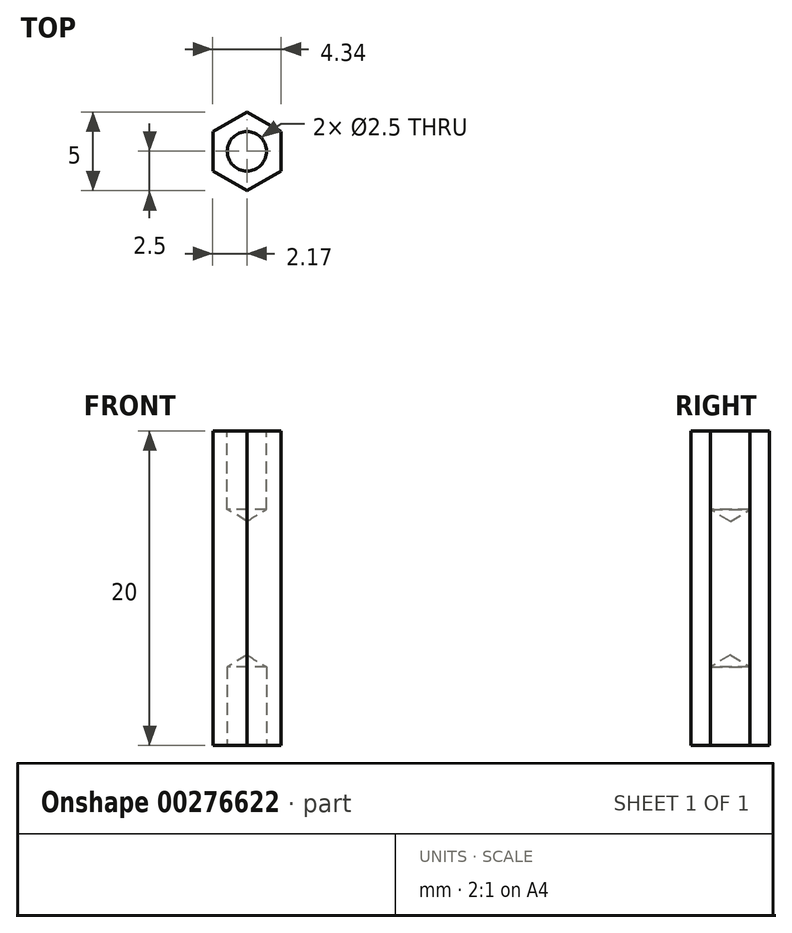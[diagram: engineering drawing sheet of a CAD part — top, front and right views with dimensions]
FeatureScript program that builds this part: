
annotation { "Feature Type Name" : "Feature", "Feature Type Description" : "" }
export const myFeature = defineFeature(function(context is Context, id is Id, definition is map)
    precondition{}
    {
        {
            var Q0;
            Q0=qCreatedBy(makeId("Top.planeOp"),FACE);
            var sketch = newSketch(context, id + "F0", { "sketchPlane" : qUnion([Q0])});
            skCircle(sketch, "E0", {"center": v(0, 0) * mm, "radius": 2.5 * mm, "construction": true});
            skLineSegment(sketch, "E1", {"start": v(0, 0) * mm, "end": v(0, 2.5) * mm});
            skCircle(sketch, "E2", {"center": v(0, 2.5) * mm, "radius": 2.5 * mm, "construction": true});
            skLineSegment(sketch, "E3", {"start": v(0, 0) * mm, "end": v(0, -2.5) * mm});
            skCircle(sketch, "E4", {"center": v(0, -2.5) * mm, "radius": 2.5 * mm, "construction": true});
            skLineSegment(sketch, "E5", {"start": v(-2.17, 1.25) * mm, "end": v(-2.17, -1.25) * mm});
            skLineSegment(sketch, "E6", {"start": v(-2.17, -1.25) * mm, "end": v(0, -2.5) * mm});
            skLineSegment(sketch, "E7", {"start": v(0, -2.5) * mm, "end": v(2.17, -1.25) * mm});
            skLineSegment(sketch, "E8", {"start": v(2.17, -1.25) * mm, "end": v(2.17, 1.25) * mm});
            skLineSegment(sketch, "E9", {"start": v(2.17, 1.25) * mm, "end": v(0, 2.5) * mm});
            skLineSegment(sketch, "E10", {"start": v(-2.17, 1.25) * mm, "end": v(0, 2.5) * mm});
            skSolve(sketch);
        }
        {
            var Q0;
            Q0 = qSketchRegion(id + "F0", true);
            extrude(context, id + "F1", {"entities" : qUnion([Q0]), "depth" : 10 * mm});
        }
        {
            var Q0;
            Q0=makeQuery(id+"F1.opExtrude","CAP_FACE",FACE,{"disambiguationData":[OSD([sQuery(id+"F0.wireOp",EDGE,"E5"),sQuery(id+"F0.wireOp",EDGE,"E6"),sQuery(id+"F0.wireOp",EDGE,"E7"),sQuery(id+"F0.wireOp",EDGE,"E8"),sQuery(id+"F0.wireOp",EDGE,"E9"),sQuery(id+"F0.wireOp",EDGE,"E10")])],"isStart":false});
            var sketch = newSketch(context, id + "F2", { "sketchPlane" : qUnion([Q0])});
            skCircle(sketch, "E11", {"center": v(0, 0) * mm, "radius": 1.08 * mm});
            skSolve(sketch);
        }
        {
            var Q0;
            Q0=sQuery(id+"F2.wireOp",VERTEX,"E11.center");
            var Q1;
            Q1=makeQuery(id+"F1.opExtrude","SWEPT_BODY",BODY,{"disambiguationData":[OSD([sQuery(id+"F0.wireOp",EDGE,"E5"),sQuery(id+"F0.wireOp",EDGE,"E6"),sQuery(id+"F0.wireOp",EDGE,"E7"),sQuery(id+"F0.wireOp",EDGE,"E8"),sQuery(id+"F0.wireOp",EDGE,"E9"),sQuery(id+"F0.wireOp",EDGE,"E10")])]});
            hole(context, id + "F3", {"style" : HoleStyle.SIMPLE, "endStyle" : HoleEndStyle.BLIND, "holeDiameter" : 2.5 * mm, "holeDepth" : 5 * mm, "tappedDepth" : 12 * mm, "tapClearance" : 3, "locations" : qUnion([Q0]), "scope" : qUnion([Q1])});
        }
        {
            var Q0;
            Q0=makeQuery(id+"F1.opExtrude","SWEPT_BODY",BODY,{"disambiguationData":[OSD([sQuery(id+"F0.wireOp",EDGE,"E5"),sQuery(id+"F0.wireOp",EDGE,"E6"),sQuery(id+"F0.wireOp",EDGE,"E7"),sQuery(id+"F0.wireOp",EDGE,"E8"),sQuery(id+"F0.wireOp",EDGE,"E9"),sQuery(id+"F0.wireOp",EDGE,"E10")])]});
            var Q1;
            Q1=qCreatedBy(makeId("Top.planeOp"),FACE);
            mirror(context, id + "F4", {"operationType" : NewBodyOperationType.ADD, "entities" : qUnion([Q0]), "mirrorPlane" : qUnion([Q1])});
        }
    });
